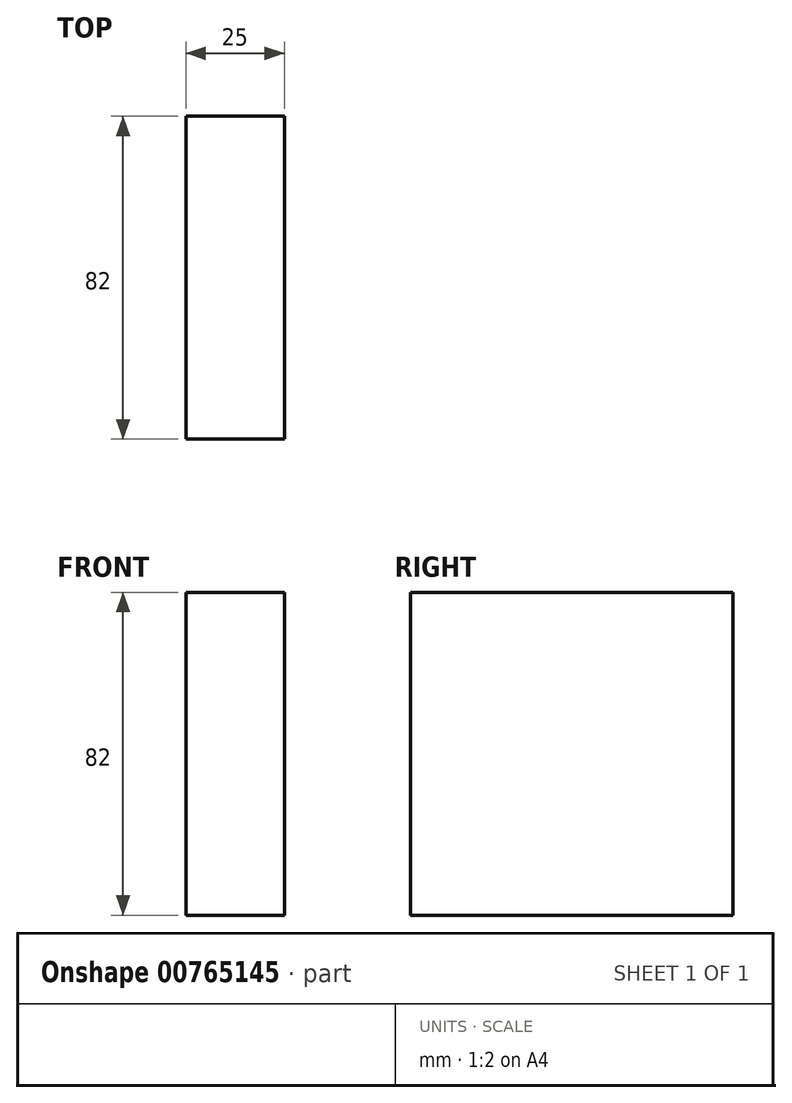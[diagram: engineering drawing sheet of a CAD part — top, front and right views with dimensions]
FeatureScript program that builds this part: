
annotation { "Feature Type Name" : "Feature", "Feature Type Description" : "" }
export const myFeature = defineFeature(function(context is Context, id is Id, definition is map)
    precondition{}
    {
        {
            var Q0;
            Q0=qCreatedBy(makeId("Right.planeOp"),FACE);
            var sketch = newSketch(context, id + "F0", { "sketchPlane" : qUnion([Q0])});
            skLineSegment(sketch, "E0.bottom", {"start": v(0, 0) * mm, "end": v(82, 0) * mm});
            skLineSegment(sketch, "E0.top", {"start": v(0, 82) * mm, "end": v(82, 82) * mm});
            skLineSegment(sketch, "E0.left", {"start": v(0, 0) * mm, "end": v(0, 82) * mm});
            skLineSegment(sketch, "E0.right", {"start": v(82, 0) * mm, "end": v(82, 82) * mm});
            skSolve(sketch);
        }
        {
            var Q0;
            Q0=makeQuery(id+"F0.imprint","IMPRINT",FACE,{"disambiguationData":[TD([[makeQuery(id+"F0.imprint","IMPRINT",EDGE,{"derivedFrom":sQuery(id+"F0.wireOp",EDGE,"E0.bottom")}),1.0]])]});
            extrude(context, id + "F1", {"entities" : qUnion([Q0]), "depth" : 25 * mm, "offsetDistance" : 25 * mm});
        }
    });
